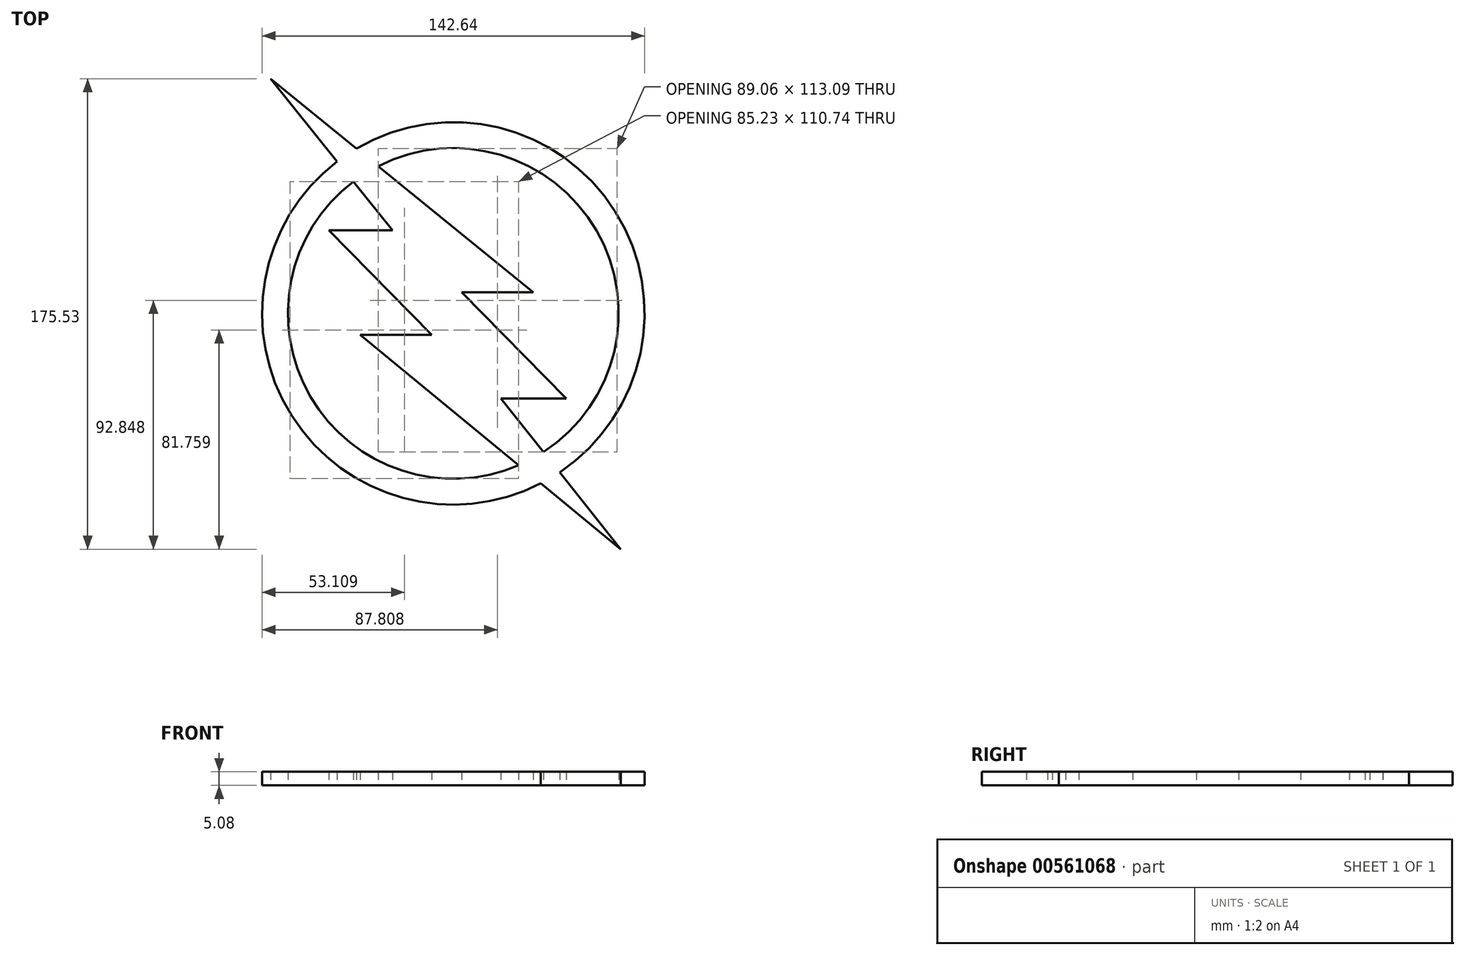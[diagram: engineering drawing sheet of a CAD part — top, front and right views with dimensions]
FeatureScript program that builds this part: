
annotation { "Feature Type Name" : "Feature", "Feature Type Description" : "" }
export const myFeature = defineFeature(function(context is Context, id is Id, definition is map)
    precondition{}
    {
        {
            var Q0;
            Q0=qCreatedBy(makeId("Top.planeOp"),FACE);
            var sketch = newSketch(context, id + "F0", { "sketchPlane" : qUnion([Q0])});
            skLineSegment(sketch, "E0", {"start": v(-62.73, 79.67) * mm, "end": v(35.14, 0) * mm});
            skLineSegment(sketch, "E1", {"start": v(35.14, 0) * mm, "end": v(8.57, 0) * mm});
            skLineSegment(sketch, "E2", {"start": v(8.57, 0) * mm, "end": v(47.52, -39.57) * mm});
            skLineSegment(sketch, "E3", {"start": v(47.52, -39.57) * mm, "end": v(23.1, -39.57) * mm});
            skLineSegment(sketch, "E4", {"start": v(23.1, -39.57) * mm, "end": v(67.89, -95.86) * mm});
            skLineSegment(sketch, "E5", {"start": v(67.89, -95.86) * mm, "end": v(-29.34, -15.83) * mm});
            skLineSegment(sketch, "E6", {"start": v(-29.34, -15.83) * mm, "end": v(-2.66, -15.83) * mm});
            skLineSegment(sketch, "E7", {"start": v(-2.66, -15.83) * mm, "end": v(-41, 23.1) * mm});
            skLineSegment(sketch, "E8", {"start": v(-41, 23.1) * mm, "end": v(-17.29, 23.1) * mm});
            skLineSegment(sketch, "E9", {"start": v(-17.29, 23.1) * mm, "end": v(-62.73, 79.67) * mm});
            skArc(sketch, "E10", {"start": v(45.03, -67.14) * mm, "mid": v(65.79, 30.04) * mm, "end": v(-30.74, 53.63) * mm});
            skArc(sketch, "E11.0", {"start": v(39, -59.56) * mm, "mid": v(58.76, 23) * mm, "end": v(-22.66, 47.05) * mm});
            skArc(sketch, "E12.trimOffspring", {"start": v(-31.88, 41.27) * mm, "mid": v(-47.9, -38.93) * mm, "end": v(29.78, -64.5) * mm});
            skArc(sketch, "E13.trimOffspring", {"start": v(-37.93, 48.8) * mm, "mid": v(-54.9, -45.99) * mm, "end": v(38.02, -71.28) * mm});
            skSolve(sketch);
        }
        {
            var Q0;
            {var subQ19=sQuery(id+"F0.wireOp",EDGE,"E1");Q0=makeQuery(id+"F0.imprint","IMPRINT",FACE,{"disambiguationData":[TD([[makeQuery(id+"F0.imprint","IMPRINT",EDGE,{"derivedFrom":subQ19}),-1.0]])]});}
            var Q1;
            {var subQ0=sQuery(id+"F0.wireOp",EDGE,"E12.trimOffspring");Q1=makeQuery(id+"F0.imprint","IMPRINT",FACE,{"disambiguationData":[TD([[makeQuery(id+"F0.imprint","IMPRINT",EDGE,{"derivedFrom":subQ0}),-1.0]])]});}
            var Q2;
            {var subQ0=sQuery(id+"F0.wireOp",EDGE,"E10");Q2=makeQuery(id+"F0.imprint","IMPRINT",FACE,{"disambiguationData":[TD([[makeQuery(id+"F0.imprint","IMPRINT",EDGE,{"derivedFrom":subQ0}),1.0]])]});}
            extrude(context, id + "F1", {"entities" : qUnion([Q0, Q1, Q2]), "depth" : 5.08 * mm, "offsetDistance" : 25.4 * mm});
        }
    });
